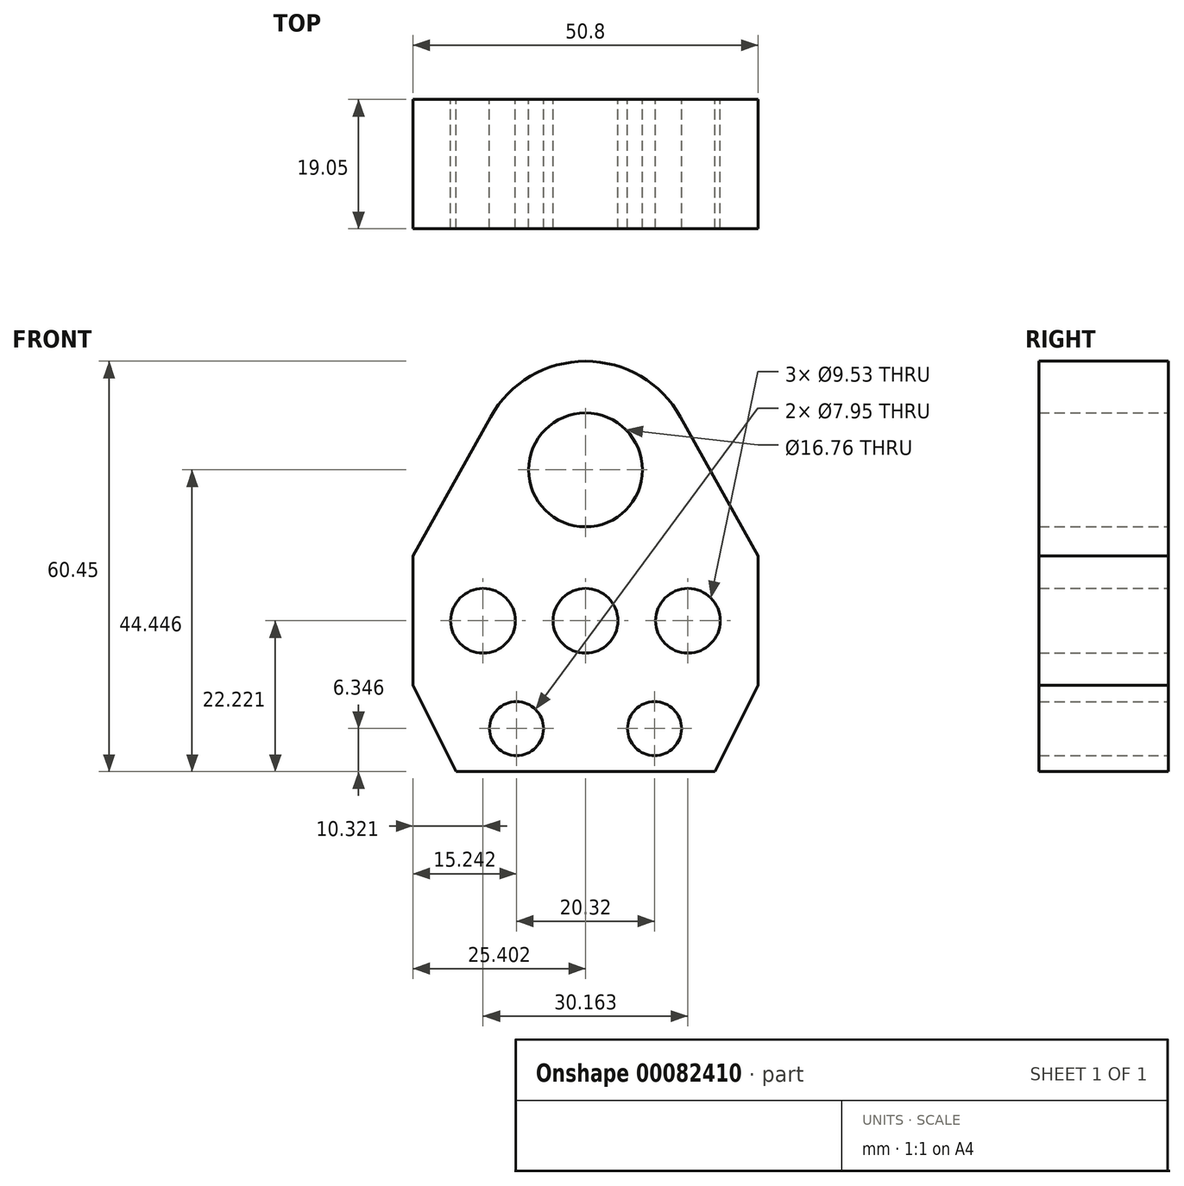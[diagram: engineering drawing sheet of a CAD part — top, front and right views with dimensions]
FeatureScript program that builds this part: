
annotation { "Feature Type Name" : "Feature", "Feature Type Description" : "" }
export const myFeature = defineFeature(function(context is Context, id is Id, definition is map)
    precondition{}
    {
        {
            var Q0;
            Q0=qCreatedBy(makeId("Front.planeOp"),FACE);
            var sketch = newSketch(context, id + "F0", { "sketchPlane" : qUnion([Q0])});
            skLineSegment(sketch, "E0.top", {"start": v(-18.35, -33.15) * mm, "end": v(19.75, -33.15) * mm});
            skLineSegment(sketch, "E0.left", {"start": v(-24.7, -1.4) * mm, "end": v(-24.7, -20.45) * mm});
            skLineSegment(sketch, "E1.0", {"start": v(-21.52, -26.8) * mm, "end": v(-13.43, -26.8) * mm});
            skArc(sketch, "E2", {"start": v(14.68, 19.09) * mm, "mid": v(0.7, 27.3) * mm, "end": v(-13.27, 19.09) * mm});
            skLineSegment(sketch, "E3", {"start": v(-24.7, -1.4) * mm, "end": v(-13.27, 19.09) * mm});
            skLineSegment(sketch, "E4", {"start": v(26.1, -1.4) * mm, "end": v(14.68, 19.09) * mm});
            skCircle(sketch, "E5", {"center": v(0.7, 11.3) * mm, "radius": 8.38 * mm});
            skLineSegment(sketch, "E6", {"start": v(19.75, -33.15) * mm, "end": v(26.1, -20.45) * mm});
            skLineSegment(sketch, "E7", {"start": v(-18.35, -33.15) * mm, "end": v(-24.7, -20.45) * mm});
            skCircle(sketch, "E8", {"center": v(-9.46, -26.8) * mm, "radius": 3.98 * mm});
            skPoint(sketch, "E9.start.orphan", {"position": v(0.7, 27.3) * mm});
            skPoint(sketch, "E10.orphan", {"position": v(26.1, -14.1) * mm});
            skPoint(sketch, "E11.orphan", {"position": v(26.1, -7.75) * mm});
            skLineSegment(sketch, "E12", {"start": v(26.1, -1.4) * mm, "end": v(26.1, -20.45) * mm});
            skPoint(sketch, "E13.orphan", {"position": v(-24.7, 27.3) * mm});
            skPoint(sketch, "E0.bottom.end.orphan", {"position": v(26.1, 27.3) * mm});
            skCircle(sketch, "E14", {"center": v(0.7, -10.93) * mm, "radius": 4.76 * mm});
            skCircle(sketch, "E15", {"center": v(15.78, -10.93) * mm, "radius": 4.76 * mm});
            skCircle(sketch, "E16", {"center": v(-14.38, -10.93) * mm, "radius": 4.76 * mm});
            skPoint(sketch, "E17.orphan", {"position": v(-24.7, -10.93) * mm});
            skPoint(sketch, "E18.trimOffspring.start.orphan", {"position": v(-4.06, -10.93) * mm});
            skPoint(sketch, "E19.orphan", {"position": v(5.46, -10.93) * mm});
            skPoint(sketch, "E20.end.orphan", {"position": v(26.1, -10.93) * mm});
            skPoint(sketch, "E21.endSnap0", {"position": v(22.93, -26.8) * mm});
            skPoint(sketch, "E22.orphan", {"position": v(15.22, -26.8) * mm});
            skPoint(sketch, "E23.orphan", {"position": v(26.1, -33.15) * mm});
            skCircle(sketch, "E24", {"center": v(10.86, -26.8) * mm, "radius": 3.98 * mm});
            skPoint(sketch, "E25.end.orphan", {"position": v(26.1, -26.8) * mm});
            skSolve(sketch);
        }
        {
            var Q0;
            {var subQ3=sQuery(id+"F0.wireOp",EDGE,"E0.left");Q0=makeQuery(id+"F0.imprint","IMPRINT",FACE,{"disambiguationData":[TD([[makeQuery(id+"F0.imprint","IMPRINT",EDGE,{"derivedFrom":subQ3}),1.0]])]});}
            extrude(context, id + "F1", {"entities" : qUnion([Q0]), "depth" : 19.05 * mm});
        }
    });
